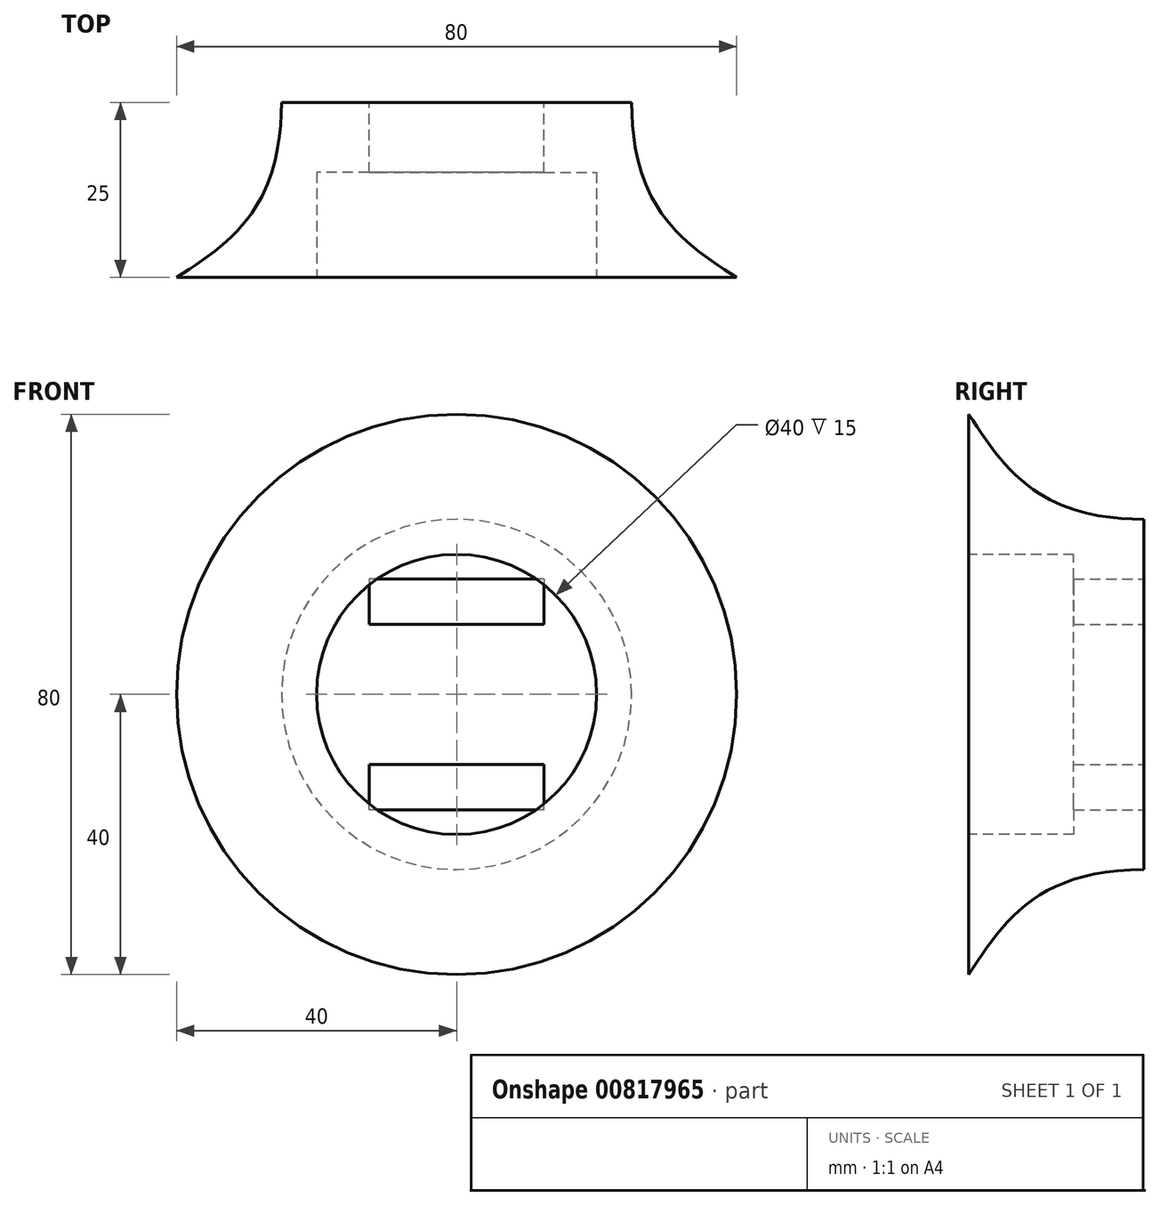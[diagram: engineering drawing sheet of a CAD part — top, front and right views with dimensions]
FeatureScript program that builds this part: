
annotation { "Feature Type Name" : "Feature", "Feature Type Description" : "" }
export const myFeature = defineFeature(function(context is Context, id is Id, definition is map)
    precondition{}
    {
        {
            var Q0;
            Q0=qCreatedBy(makeId("Front.planeOp"),FACE);
            var sketch = newSketch(context, id + "F0", { "sketchPlane" : qUnion([Q0])});
            skCircle(sketch, "E0", {"center": v(0, 0) * mm, "radius": 25 * mm});
            skSolve(sketch);
        }
        {
            var Q0;
            Q0=qCreatedBy(makeId("Front.planeOp"),FACE);
            cPlane(context, id + "F1", {"entities" : qUnion([Q0]), "cplaneType" : CPlaneType.OFFSET, "offset" : 25 * mm, "width" : 150 * mm, "height" : 150 * mm});
        }
        {
            var Q0;
            Q0=qCreatedBy(id+"F1.planeOp",FACE);
            var sketch = newSketch(context, id + "F2", { "sketchPlane" : qUnion([Q0])});
            skCircle(sketch, "E1", {"center": v(0, 0) * mm, "radius": 40 * mm});
            skSolve(sketch);
        }
        {
            var Q0;
            Q0 = qSketchRegion(id + "F0", true);
            var Q1;
            Q1 = qSketchRegion(id + "F2", true);
            loft(context, id + "F3", {"startCondition" : LoftEndDerivativeType.NORMAL_TO_PROFILE, "startMagnitude" : 1.8, "sheetProfilesArray" : [{ "sheetProfileEntities" : qUnion([Q0]) }, { "sheetProfileEntities" : qUnion([Q1]) }]});
        }
        {
            var Q0;
            Q0=makeQuery(id+"F0.imprint","IMPRINT",FACE,{"disambiguationData":[TD([[makeQuery(id+"F0.imprint","IMPRINT",EDGE,{"derivedFrom":sQuery(id+"F0.wireOp",EDGE,"E0")}),1.0]])]});
            var sketch = newSketch(context, id + "F4", { "sketchPlane" : qUnion([Q0])});
            skLineSegment(sketch, "E2.bottom", {"start": v(12.5, 16.5) * mm, "end": v(-12.5, 16.5) * mm});
            skLineSegment(sketch, "E2.top", {"start": v(12.5, 10) * mm, "end": v(-12.5, 10) * mm});
            skLineSegment(sketch, "E2.left", {"start": v(12.5, 16.5) * mm, "end": v(12.5, 10) * mm});
            skLineSegment(sketch, "E2.right", {"start": v(-12.5, 16.5) * mm, "end": v(-12.5, 10) * mm});
            skPoint(sketch, "E2.middle", {"position": v(0, 13.25) * mm});
            skLineSegment(sketch, "E3", {"start": v(16.64, 0) * mm, "end": v(0, 0) * mm});
            skLineSegment(sketch, "E4.MirrorCS", {"start": v(12.5, -10) * mm, "end": v(-12.5, -10) * mm});
            skLineSegment(sketch, "E5.MirrorCS", {"start": v(12.5, -16.5) * mm, "end": v(-12.5, -16.5) * mm});
            skLineSegment(sketch, "E6.MirrorCS", {"start": v(-12.5, -16.5) * mm, "end": v(-12.5, -10) * mm});
            skLineSegment(sketch, "E7.MirrorCS", {"start": v(12.5, -16.5) * mm, "end": v(12.5, -10) * mm});
            skSolve(sketch);
        }
        {
            var Q0;
            Q0 = qSketchRegion(id + "F4", true);
            extrude(context, id + "F5", {"entities" : qUnion([Q0]), "operationType" : NewBodyOperationType.REMOVE, "depth" : 10 * mm, "offsetDistance" : 25 * mm});
        }
        {
            var Q0;
            Q0=makeQuery(id+"F3.opLoft","CAP_FACE",FACE,{"disambiguationData":[OSD([makeQuery(id+"F2.imprint","IMPRINT",FACE,{"disambiguationData":[TD([[makeQuery(id+"F2.imprint","IMPRINT",EDGE,{"derivedFrom":sQuery(id+"F2.wireOp",EDGE,"E1")}),1.0]])]})])],"isStart":true});
            var sketch = newSketch(context, id + "F6", { "sketchPlane" : qUnion([Q0])});
            skCircle(sketch, "E8", {"center": v(0, 0) * mm, "radius": 20 * mm});
            skSolve(sketch);
        }
        {
            var Q0;
            Q0 = qSketchRegion(id + "F6", true);
            extrude(context, id + "F7", {"entities" : qUnion([Q0]), "operationType" : NewBodyOperationType.REMOVE, "oppositeDirection" : true, "depth" : 15 * mm, "offsetDistance" : 25 * mm});
        }
    });
